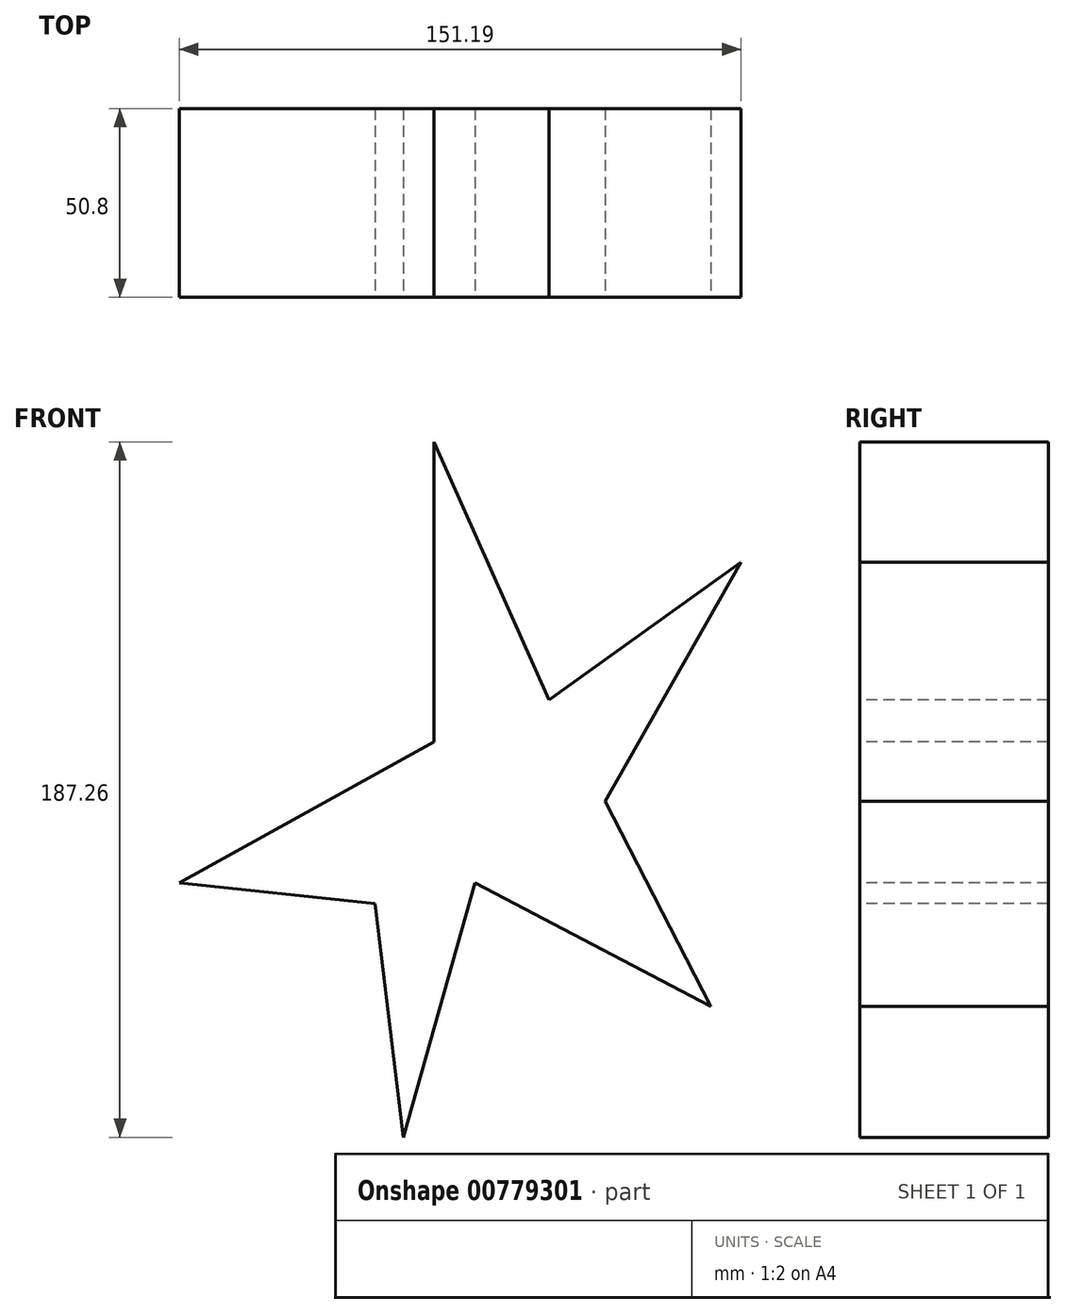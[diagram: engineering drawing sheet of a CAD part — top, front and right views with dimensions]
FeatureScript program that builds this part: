
annotation { "Feature Type Name" : "Feature", "Feature Type Description" : "" }
export const myFeature = defineFeature(function(context is Context, id is Id, definition is map)
    precondition{}
    {
        {
            var Q0;
            Q0=qCreatedBy(makeId("Front.planeOp"),FACE);
            var sketch = newSketch(context, id + "F0", { "sketchPlane" : qUnion([Q0])});
            skLineSegment(sketch, "E0", {"start": v(0, 0) * mm, "end": v(0, 80.75) * mm});
            skLineSegment(sketch, "E1", {"start": v(0, 80.75) * mm, "end": v(30.94, 11.35) * mm});
            skLineSegment(sketch, "E2", {"start": v(30.94, 11.35) * mm, "end": v(82.59, 48.32) * mm});
            skLineSegment(sketch, "E3", {"start": v(82.59, 48.32) * mm, "end": v(46, -16.04) * mm});
            skLineSegment(sketch, "E4", {"start": v(46, -16.04) * mm, "end": v(74.52, -71.3) * mm});
            skLineSegment(sketch, "E5", {"start": v(74.52, -71.3) * mm, "end": v(11.03, -37.97) * mm});
            skLineSegment(sketch, "E6", {"start": v(11.03, -37.97) * mm, "end": v(-8.34, -106.51) * mm});
            skLineSegment(sketch, "E7", {"start": v(-8.34, -106.51) * mm, "end": v(-15.87, -43.59) * mm});
            skLineSegment(sketch, "E8", {"start": v(-15.87, -43.59) * mm, "end": v(-68.6, -37.97) * mm});
            skLineSegment(sketch, "E9", {"start": v(-68.6, -37.97) * mm, "end": v(0, 0) * mm});
            skSolve(sketch);
        }
        {
            var Q0;
            Q0=makeQuery(id+"F0.imprint","IMPRINT",FACE,{"disambiguationData":[TD([[makeQuery(id+"F0.imprint","IMPRINT",EDGE,{"derivedFrom":sQuery(id+"F0.wireOp",EDGE,"E0")}),-1.0]])]});
            extrude(context, id + "F1", {"entities" : qUnion([Q0]), "oppositeDirection" : true, "depth" : 50.8 * mm, "offsetDistance" : 25.4 * mm});
        }
    });
